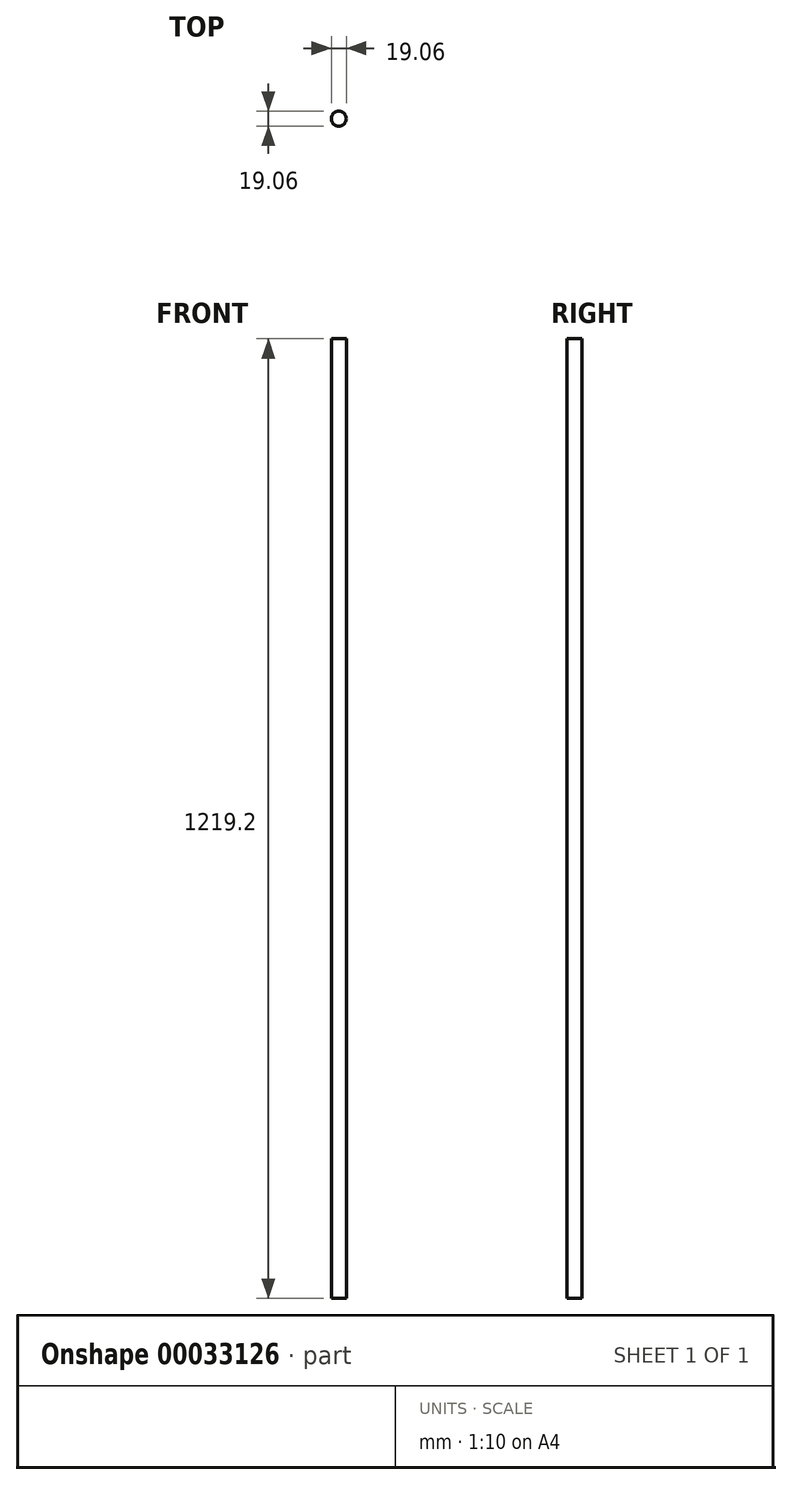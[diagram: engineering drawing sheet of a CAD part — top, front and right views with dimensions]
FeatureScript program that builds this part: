
annotation { "Feature Type Name" : "Feature", "Feature Type Description" : "" }
export const myFeature = defineFeature(function(context is Context, id is Id, definition is map)
    precondition{}
    {
        {
            var Q0;
            Q0=qCreatedBy(makeId("Top.planeOp"),FACE);
            var sketch = newSketch(context, id + "F0", { "sketchPlane" : qUnion([Q0])});
            skCircle(sketch, "E0", {"center": v(0, 0) * mm, "radius": 9.53 * mm});
            skSolve(sketch);
        }
        {
            var Q0;
            Q0 = qSketchRegion(id + "F0", true);
            extrude(context, id + "F1", {"entities" : qUnion([Q0]), "depth" : 1219.2 * mm});
        }
    });
